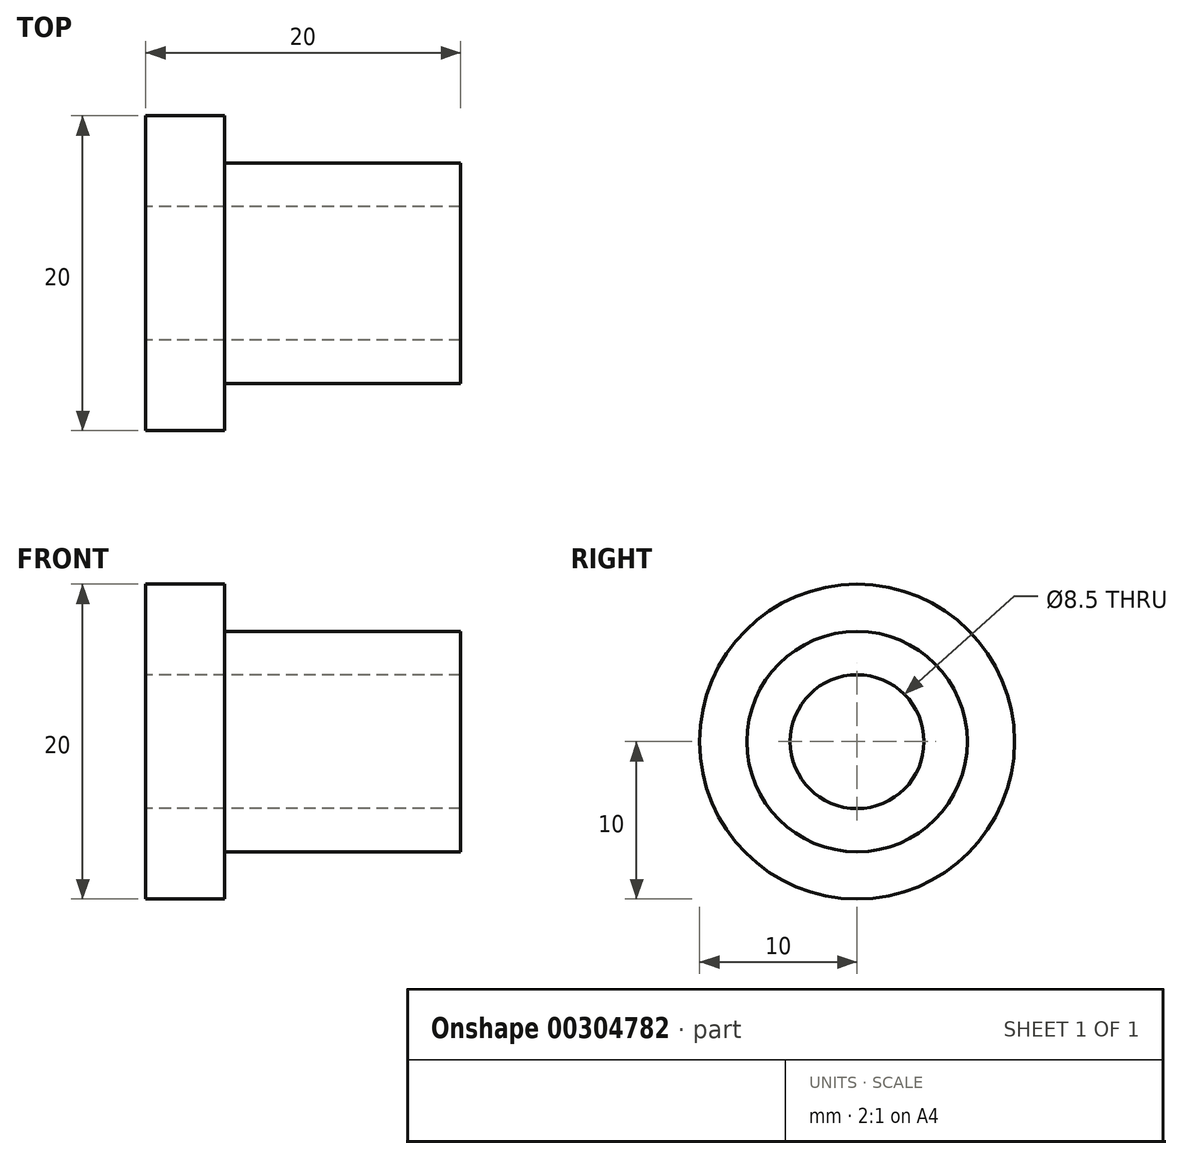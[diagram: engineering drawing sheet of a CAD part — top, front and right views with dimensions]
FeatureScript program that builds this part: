
annotation { "Feature Type Name" : "Feature", "Feature Type Description" : "" }
export const myFeature = defineFeature(function(context is Context, id is Id, definition is map)
    precondition{}
    {
        {
            var Q0;
            Q0=qCreatedBy(makeId("Top.planeOp"),FACE);
            var sketch = newSketch(context, id + "F0", { "sketchPlane" : qUnion([Q0])});
            skLineSegment(sketch, "E0", {"start": v(0, 4.25) * mm, "end": v(0, 10) * mm});
            skLineSegment(sketch, "E1", {"start": v(0, 10) * mm, "end": v(5, 10) * mm});
            skLineSegment(sketch, "E2", {"start": v(5, 10) * mm, "end": v(5, 7) * mm});
            skLineSegment(sketch, "E3", {"start": v(5, 7) * mm, "end": v(20, 7) * mm});
            skLineSegment(sketch, "E4", {"start": v(20, 4.25) * mm, "end": v(0, 4.25) * mm});
            skLineSegment(sketch, "E5", {"start": v(20, 7) * mm, "end": v(20, 4.25) * mm});
            skLineSegment(sketch, "E6", {"start": v(-52.03, 0) * mm, "end": v(151.17, 0) * mm, "construction": true});
            skSolve(sketch);
        }
        {
            var Q0;
            Q0=makeQuery(id+"F0.imprint","IMPRINT",FACE,{"disambiguationData":[TD([[makeQuery(id+"F0.imprint","IMPRINT",EDGE,{"derivedFrom":sQuery(id+"F0.wireOp",EDGE,"E0")}),-1.0]])]});
            var Q1;
            Q1=sQuery(id+"F0.wireOp",EDGE,"E6");
            revolve(context, id + "F1", {"surfaceOperationType" : NewSurfaceOperationType.NEW, "entities" : qUnion([Q0]), "axis" : qUnion([Q1]), "revolveType" : RevolveType.FULL});
        }
    });
